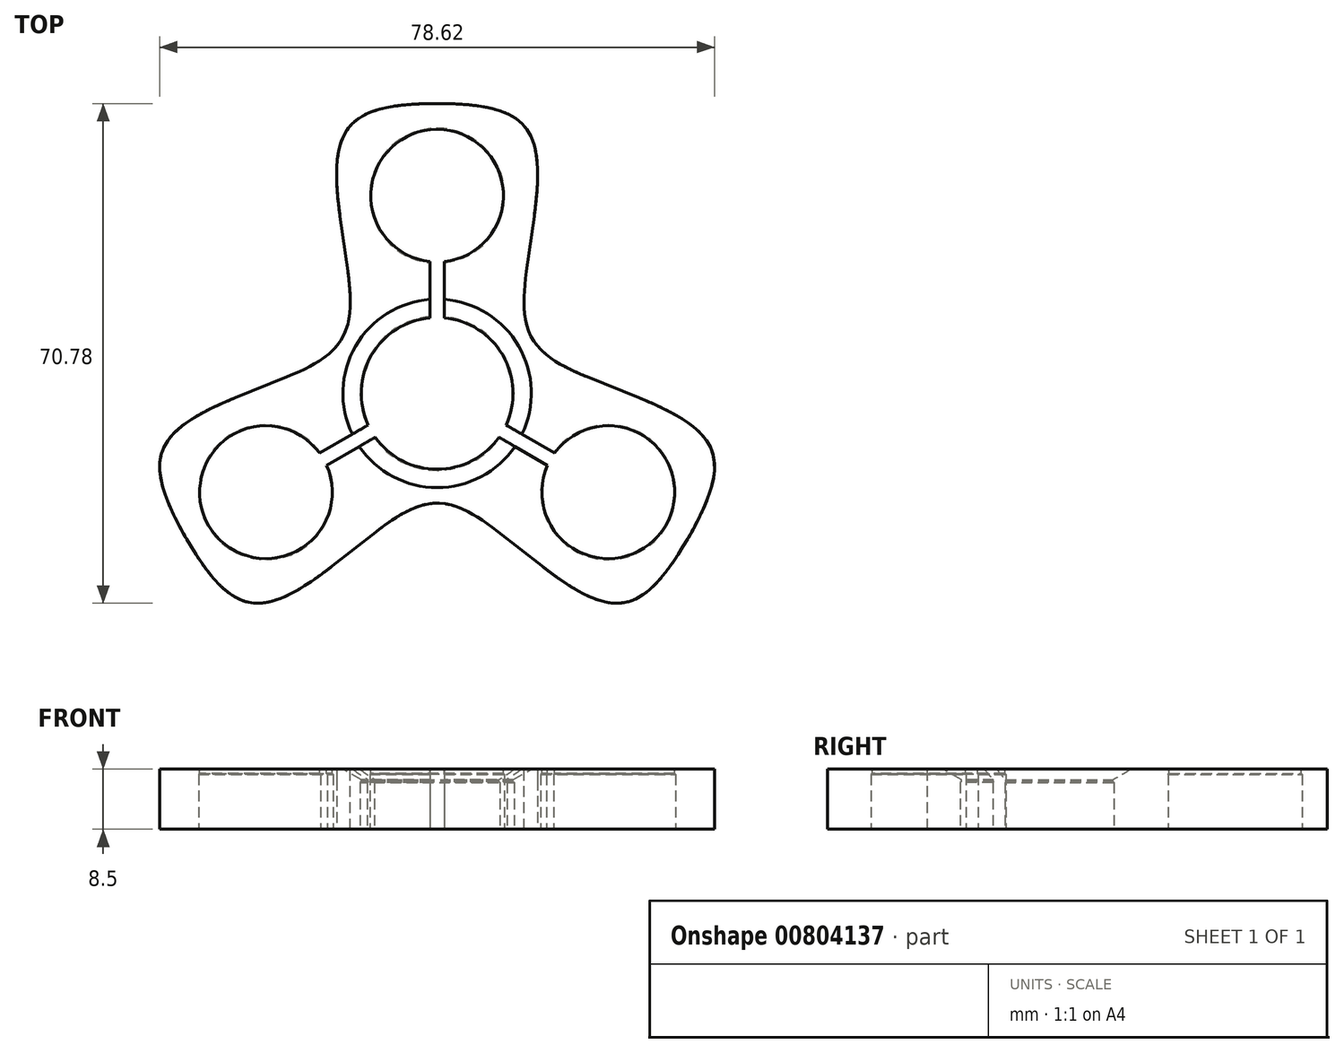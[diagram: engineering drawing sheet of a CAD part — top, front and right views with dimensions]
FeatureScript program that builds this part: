
annotation { "Feature Type Name" : "Feature", "Feature Type Description" : "" }
export const myFeature = defineFeature(function(context is Context, id is Id, definition is map)
    precondition{}
    {
        {
            var Q0;
            Q0=qCreatedBy(makeId("Top.planeOp"),FACE);
            var sketch = newSketch(context, id + "F0", { "sketchPlane" : qUnion([Q0])});
            skLineSegment(sketch, "E0", {"start": v(0, 0) * mm, "end": v(71.1, 41.05) * mm, "construction": true});
            skLineSegment(sketch, "E1", {"start": v(0, 0) * mm, "end": v(-71.1, 41.05) * mm, "construction": true});
            skCircle(sketch, "E2", {"center": v(0, 0) * mm, "radius": 10.9 * mm, "construction": true});
            skCircle(sketch, "E3", {"center": v(0, 28) * mm, "radius": 9.55 * mm});
            skLineSegment(sketch, "E4", {"start": v(-16, 41.05) * mm, "end": v(16, 41.05) * mm});
            skLineSegment(sketch, "E5", {"start": v(16, 41.05) * mm, "end": v(11.13, 6.43) * mm});
            skLineSegment(sketch, "E6", {"start": v(-16, 41.05) * mm, "end": v(-11.13, 6.43) * mm});
            skLineSegment(sketch, "E7", {"start": v(0, 28) * mm, "end": v(0, 41.05) * mm, "construction": true});
            skPoint(sketch, "E8", {"position": v(0, 37.55) * mm});
            skArc(sketch, "E9", {"start": v(9.44, 5.45) * mm, "mid": v(0, 10.9) * mm, "end": v(-9.44, 5.45) * mm});
            skLineSegment(sketch, "E10", {"start": v(-9.44, 5.45) * mm, "end": v(-11.13, 6.43) * mm});
            skLineSegment(sketch, "E11", {"start": v(9.44, 5.45) * mm, "end": v(11.13, 6.43) * mm});
            skSolve(sketch);
        }
        {
            var Q0;
            Q0=qSketchRegion(id+"F0",true);
            extrude(context, id + "F1", {"entities" : qUnion([Q0]), "endBound" : BoundingType.SYMMETRIC, "depth" : 7 * mm, "offsetDistance" : 25 * mm});
        }
        {
            var Q0;
            Q0=makeQuery(id+"F1.opExtrude","SWEPT_EDGE",EDGE,{"disambiguationData":[OSD([sQuery(id+"F0.wireOp",EDGE,"E4"),sQuery(id+"F0.wireOp",EDGE,"E6")])]});
            var Q1;
            Q1=makeQuery(id+"F1.opExtrude","SWEPT_EDGE",EDGE,{"disambiguationData":[OSD([sQuery(id+"F0.wireOp",EDGE,"E4"),sQuery(id+"F0.wireOp",EDGE,"E5")])]});
            fillet(context, id + "F2", {"entities" : qUnion([Q0, Q1]), "radius" : 14 * mm, "tangentPropagation" : true, "rho" : .6, "crossSection" : FilletCrossSection.CONIC, "allowEdgeOverflow" : false});
        }
        {
            var Q0;
            Q0=makeQuery(id+"F1.opExtrude","CAP_FACE",FACE,{"disambiguationData":[OSD([sQuery(id+"F0.wireOp",EDGE,"E3"),sQuery(id+"F0.wireOp",EDGE,"E4"),sQuery(id+"F0.wireOp",EDGE,"E5"),sQuery(id+"F0.wireOp",EDGE,"E6"),sQuery(id+"F0.wireOp",EDGE,"E9"),sQuery(id+"F0.wireOp",EDGE,"E10"),sQuery(id+"F0.wireOp",EDGE,"E11")])],"isStart":false});
            var sketch = newSketch(context, id + "F3", { "sketchPlane" : qUnion([Q0])});
            skCircle(sketch, "E12.0", {"center": v(0, 28) * mm, "radius": 9.55 * mm});
            skCircle(sketch, "E13.0", {"center": v(0, 28) * mm, "radius": 9.4 * mm});
            skArc(sketch, "E14.0", {"start": v(9.44, 5.45) * mm, "mid": v(0, 10.9) * mm, "end": v(-9.44, 5.45) * mm});
            skArc(sketch, "E15.0", {"start": v(9.3, 5.37) * mm, "mid": v(0, 10.75) * mm, "end": v(-9.3, 5.37) * mm});
            skLineSegment(sketch, "E16", {"start": v(-9.3, 5.37) * mm, "end": v(-9.44, 5.45) * mm});
            skLineSegment(sketch, "E17", {"start": v(9.3, 5.37) * mm, "end": v(9.44, 5.45) * mm});
            skSolve(sketch);
        }
        {
            var Q0;
            Q0=makeQuery(id+"F3.imprint","IMPRINT",FACE,{"disambiguationData":[TD([[makeQuery(id+"F3.imprint","IMPRINT",EDGE,{"derivedFrom":sQuery(id+"F3.wireOp",EDGE,"E14.0")}),1.0]])]});
            extrude(context, id + "F4", {"entities" : qUnion([Q0]), "operationType" : NewBodyOperationType.ADD, "oppositeDirection" : true, "depth" : .4 * mm, "offsetDistance" : 25 * mm});
        }
        {
            var Q0;
            Q0=makeQuery(id+"F4.boolean.opBoolean","MERGE",FACE,{"derivedFrom":[makeQuery(id+"F1.opExtrude","CAP_FACE",FACE,{"disambiguationData":[OSD([sQuery(id+"F0.wireOp",EDGE,"E3"),sQuery(id+"F0.wireOp",EDGE,"E4"),sQuery(id+"F0.wireOp",EDGE,"E5"),sQuery(id+"F0.wireOp",EDGE,"E6"),sQuery(id+"F0.wireOp",EDGE,"E9"),sQuery(id+"F0.wireOp",EDGE,"E10"),sQuery(id+"F0.wireOp",EDGE,"E11")])],"isStart":false}),makeQuery(id+"F4.opExtrude","CAP_FACE",FACE,{"disambiguationData":[OSD([sQuery(id+"F3.wireOp",EDGE,"E14.0"),sQuery(id+"F3.wireOp",EDGE,"E15.0"),sQuery(id+"F3.wireOp",EDGE,"E16"),sQuery(id+"F3.wireOp",EDGE,"E17")])],"isStart":true})]});
            extrude(context, id + "F5", {"entities" : qUnion([Q0]), "operationType" : NewBodyOperationType.ADD, "depth" : 1.5 * mm, "offsetDistance" : 25 * mm});
        }
        {
            var Q0;
            Q0=makeQuery(id+"F5.opExtrude","CAP_FACE",FACE,{"disambiguationData":[OSD([sQuery(id+"F0.wireOp",EDGE,"E3"),sQuery(id+"F0.wireOp",EDGE,"E4"),sQuery(id+"F0.wireOp",EDGE,"E5"),sQuery(id+"F0.wireOp",EDGE,"E6"),sQuery(id+"F0.wireOp",EDGE,"E9"),sQuery(id+"F0.wireOp",EDGE,"E10"),sQuery(id+"F0.wireOp",EDGE,"E11"),sQuery(id+"F3.wireOp",EDGE,"E14.0"),sQuery(id+"F3.wireOp",EDGE,"E15.0"),sQuery(id+"F3.wireOp",EDGE,"E16"),sQuery(id+"F3.wireOp",EDGE,"E17")])],"isStart":false});
            var sketch = newSketch(context, id + "F6", { "sketchPlane" : qUnion([Q0])});
            skCircle(sketch, "E18.0", {"center": v(0, 28) * mm, "radius": 9.4 * mm});
            skCircle(sketch, "E19.0", {"center": v(0, 28) * mm, "radius": 9.55 * mm});
            skSolve(sketch);
        }
        {
            var Q0;
            Q0=qSketchRegion(id+"F6",true);
            extrude(context, id + "F7", {"entities" : qUnion([Q0]), "operationType" : NewBodyOperationType.ADD, "oppositeDirection" : true, "depth" : .75 * mm, "offsetDistance" : 25 * mm});
        }
        {
            var Q0;
            Q0=makeQuery(id+"F4.opExtrude","CAP_EDGE",EDGE,{"disambiguationData":[OSD([sQuery(id+"F3.wireOp",EDGE,"E13.0")])],"isStart":false});
            var Q1;
            Q1=makeQuery(id+"F4.opExtrude","CAP_EDGE",EDGE,{"disambiguationData":[OSD([sQuery(id+"F3.wireOp",EDGE,"E15.0")])],"isStart":false});
            var Q2;
            Q2=makeQuery(id+"F7.opExtrude","CAP_EDGE",EDGE,{"disambiguationData":[OSD([sQuery(id+"F6.wireOp",EDGE,"E18.0")])],"isStart":false});
            chamfer(context, id + "F8", {"entities" : qUnion([Q0, Q1, Q2]), "width" : .15 * mm, "tangentPropagation" : true});
        }
        {
            var Q0;
            Q0=makeQuery(id+"F5.opExtrude","CAP_EDGE",EDGE,{"disambiguationData":[OSD([sQuery(id+"F3.wireOp",EDGE,"E15.0")])],"isStart":false});
            chamfer(context, id + "F9", {"entities" : qUnion([Q0]), "chamferType" : ChamferType.OFFSET_ANGLE, "width" : 1.5 * mm, "oppositeDirection" : false, "angle" : 60 * degree, "tangentPropagation" : true});
        }
        {
            var Q0;
            Q0=qCreatedBy(makeId("Top.planeOp"),FACE);
            var sketch = newSketch(context, id + "F10", { "sketchPlane" : qUnion([Q0])});
            skLineSegment(sketch, "E20.bottom", {"start": v(-1, 0) * mm, "end": v(1, 0) * mm});
            skLineSegment(sketch, "E20.top", {"start": v(-1, 28) * mm, "end": v(1, 28) * mm});
            skLineSegment(sketch, "E20.left", {"start": v(-1, 0) * mm, "end": v(-1, 28) * mm});
            skLineSegment(sketch, "E20.right", {"start": v(1, 0) * mm, "end": v(1, 28) * mm});
            skPoint(sketch, "E21", {"position": v(0, 28) * mm});
            skSolve(sketch);
        }
        {
            var Q0;
            Q0=makeQuery(id+"F10.imprint","IMPRINT",FACE,{"disambiguationData":[TD([[makeQuery(id+"F10.imprint","IMPRINT",EDGE,{"derivedFrom":sQuery(id+"F10.wireOp",EDGE,"E20.bottom")}),1.0]])]});
            extrude(context, id + "F11", {"entities" : qUnion([Q0]), "operationType" : NewBodyOperationType.REMOVE, "endBound" : BoundingType.THROUGH_ALL, "depth" : 25 * mm, "offsetDistance" : 25 * mm, "hasSecondDirection" : true, "secondDirectionBound" : SecondDirectionBoundingType.THROUGH_ALL, "secondDirectionOppositeDirection" : true, "secondDirectionDepth" : 25 * mm});
        }
        {
            var Q0;
            Q0=qCreatedBy(makeId("Front.planeOp"),FACE);
            var sketch = newSketch(context, id + "F12", { "sketchPlane" : qUnion([Q0])});
            skLineSegment(sketch, "E22", {"start": v(0, 0) * mm, "end": v(0, 20.55) * mm, "construction": true});
            skSolve(sketch);
        }
        {
            var Q0;
            Q0=makeQuery(id+"F1.opExtrude","SWEPT_BODY",BODY,{"disambiguationData":[OSD([sQuery(id+"F0.wireOp",EDGE,"E3"),sQuery(id+"F0.wireOp",EDGE,"E4"),sQuery(id+"F0.wireOp",EDGE,"E5"),sQuery(id+"F0.wireOp",EDGE,"E6"),sQuery(id+"F0.wireOp",EDGE,"E9"),sQuery(id+"F0.wireOp",EDGE,"E10"),sQuery(id+"F0.wireOp",EDGE,"E11")])]});
            var Q1;
            Q1=sQuery(id+"F12.wireOp",EDGE,"E22");
            circularPattern(context, id + "F13", {"operationType" : NewBodyOperationType.ADD, "entities" : qUnion([Q0]), "axis" : qUnion([Q1]), "angle" : 360 * degree, "instanceCount" : 3, "equalSpace" : true});
        }
        {
            var Q0;
            Q0=makeQuery(id+"F13.boolean.opBoolean","MERGE",EDGE,{"derivedFrom":[makeQuery(id+"F1.opExtrude","SWEPT_EDGE",EDGE,{"disambiguationData":[OSD([sQuery(id+"F0.wireOp",EDGE,"E5"),sQuery(id+"F0.wireOp",EDGE,"E11")])]}),makeQuery(id+"F13.opPattern","COPY",EDGE,{"derivedFrom":makeQuery(id+"F1.opExtrude","SWEPT_EDGE",EDGE,{"disambiguationData":[OSD([sQuery(id+"F0.wireOp",EDGE,"E6"),sQuery(id+"F0.wireOp",EDGE,"E10")])]}),"instanceName":"2"})]});
            var Q1;
            Q1=makeQuery(id+"F13.boolean.opBoolean","MERGE",EDGE,{"derivedFrom":[makeQuery(id+"F1.opExtrude","SWEPT_EDGE",EDGE,{"disambiguationData":[OSD([sQuery(id+"F0.wireOp",EDGE,"E6"),sQuery(id+"F0.wireOp",EDGE,"E10")])]}),makeQuery(id+"F13.opPattern","COPY",EDGE,{"derivedFrom":makeQuery(id+"F1.opExtrude","SWEPT_EDGE",EDGE,{"disambiguationData":[OSD([sQuery(id+"F0.wireOp",EDGE,"E5"),sQuery(id+"F0.wireOp",EDGE,"E11")])]}),"instanceName":"1"})]});
            var Q2;
            Q2=makeQuery(id+"F13.boolean.opBoolean","MERGE",EDGE,{"derivedFrom":[makeQuery(id+"F13.opPattern","COPY",EDGE,{"derivedFrom":makeQuery(id+"F1.opExtrude","SWEPT_EDGE",EDGE,{"disambiguationData":[OSD([sQuery(id+"F0.wireOp",EDGE,"E6"),sQuery(id+"F0.wireOp",EDGE,"E10")])]}),"instanceName":"1"}),makeQuery(id+"F13.opPattern","COPY",EDGE,{"derivedFrom":makeQuery(id+"F1.opExtrude","SWEPT_EDGE",EDGE,{"disambiguationData":[OSD([sQuery(id+"F0.wireOp",EDGE,"E5"),sQuery(id+"F0.wireOp",EDGE,"E11")])]}),"instanceName":"2"})]});
            fillet(context, id + "F14", {"entities" : qUnion([Q0, Q1, Q2]), "radius" : 14 * mm, "tangentPropagation" : true, "rho" : .6, "crossSection" : FilletCrossSection.CONIC, "allowEdgeOverflow" : false});
        }
    });
